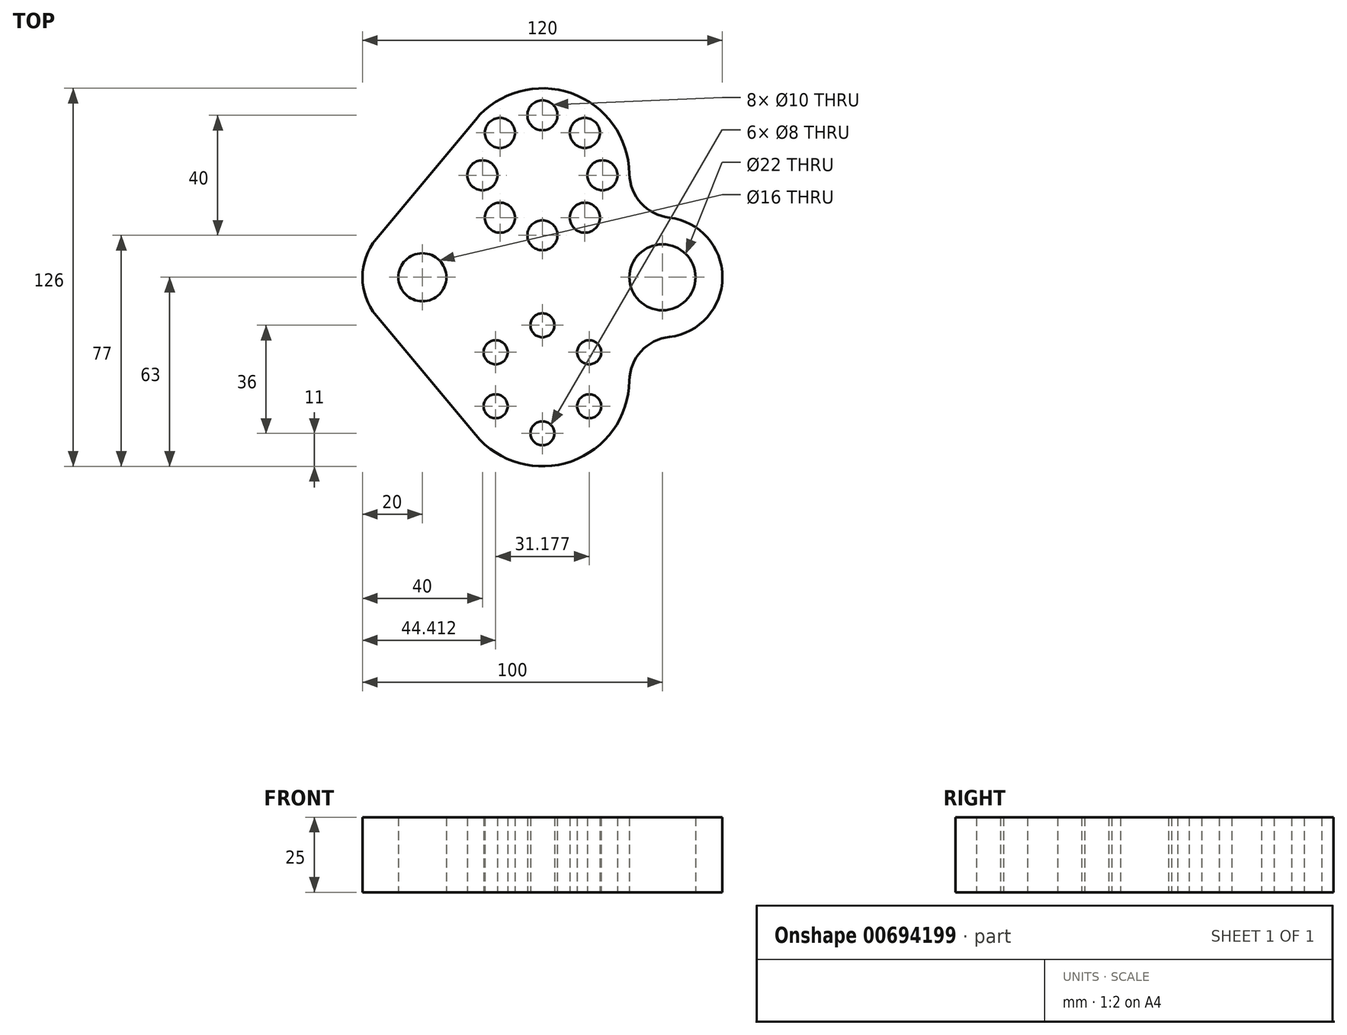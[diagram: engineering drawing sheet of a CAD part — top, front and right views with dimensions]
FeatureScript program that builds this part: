
annotation { "Feature Type Name" : "Feature", "Feature Type Description" : "" }
export const myFeature = defineFeature(function(context is Context, id is Id, definition is map)
    precondition{}
    {
        {
            var Q0;
            Q0=qCreatedBy(makeId("Top.planeOp"),FACE);
            var sketch = newSketch(context, id + "F0", { "sketchPlane" : qUnion([Q0])});
            skCircle(sketch, "E0", {"center": v(0, 34) * mm, "radius": 29 * mm});
            skCircle(sketch, "E1.MirrorC", {"center": v(0, -34) * mm, "radius": 29 * mm});
            skCircle(sketch, "E2", {"center": v(0, 54) * mm, "radius": 5 * mm});
            skCircle(sketch, "E3.1.0", {"center": v(-14.14, 48.14) * mm, "radius": 5 * mm});
            skCircle(sketch, "E3.2.0", {"center": v(-20, 34) * mm, "radius": 5 * mm});
            skCircle(sketch, "E3.3.0", {"center": v(-14.14, 19.86) * mm, "radius": 5 * mm});
            skCircle(sketch, "E3.4.0", {"center": v(0, 14) * mm, "radius": 5 * mm});
            skCircle(sketch, "E3.5.0", {"center": v(14.14, 19.86) * mm, "radius": 5 * mm});
            skCircle(sketch, "E3.6.0", {"center": v(20, 34) * mm, "radius": 5 * mm});
            skCircle(sketch, "E3.7.0", {"center": v(14.14, 48.14) * mm, "radius": 5 * mm});
            skLineSegment(sketch, "E4", {"start": v(0, -48) * mm, "end": v(0, -52) * mm});
            skCircle(sketch, "E5", {"center": v(0, -52) * mm, "radius": 4 * mm});
            skCircle(sketch, "E6.1.0", {"center": v(15.59, -43) * mm, "radius": 4 * mm});
            skCircle(sketch, "E6.2.0", {"center": v(15.59, -25) * mm, "radius": 4 * mm});
            skCircle(sketch, "E6.3.0", {"center": v(0, -16) * mm, "radius": 4 * mm});
            skCircle(sketch, "E6.4.0", {"center": v(-15.59, -25) * mm, "radius": 4 * mm});
            skCircle(sketch, "E6.5.0", {"center": v(-15.59, -43) * mm, "radius": 4 * mm});
            skCircle(sketch, "E7", {"center": v(-40, 0) * mm, "radius": 8 * mm});
            skArc(sketch, "E8", {"start": v(-55.37, 12.8) * mm, "mid": v(-60, 0) * mm, "end": v(-55.37, -12.8) * mm});
            skLineSegment(sketch, "E9", {"start": v(-55.37, 12.8) * mm, "end": v(-22.3, 52.55) * mm});
            skLineSegment(sketch, "E10.MirrorCS", {"start": v(-55.37, -12.8) * mm, "end": v(-22.3, -52.55) * mm});
            skCircle(sketch, "E11", {"center": v(40, 0) * mm, "radius": 11 * mm});
            skArc(sketch, "E12", {"start": v(42.28, -19.87) * mm, "mid": v(60, 0) * mm, "end": v(42.28, 19.87) * mm});
            skArc(sketch, "E13", {"start": v(29, 34.5) * mm, "mid": v(32.89, 24.7) * mm, "end": v(42.28, 19.87) * mm});
            skArc(sketch, "E14.MirrorCS", {"start": v(29, -34.5) * mm, "mid": v(32.89, -24.7) * mm, "end": v(42.28, -19.87) * mm});
            skSolve(sketch);
        }
        {
            var Q0;
            Q0=makeQuery(id+"F0.imprint","IMPRINT",FACE,{"disambiguationData":[TD([[makeQuery(id+"F0.imprint","IMPRINT",EDGE,{"derivedFrom":sQuery(id+"F0.wireOp",EDGE,"E7")}),-1.0]])]});
            var Q1;
            Q1=makeQuery(id+"F0.imprint","IMPRINT",FACE,{"disambiguationData":[TD([[makeQuery(id+"F0.imprint","IMPRINT",EDGE,{"derivedFrom":sQuery(id+"F0.wireOp",EDGE,"E5")}),-1.0]])]});
            var Q2;
            Q2=makeQuery(id+"F0.imprint","IMPRINT",FACE,{"disambiguationData":[TD([[makeQuery(id+"F0.imprint","IMPRINT",EDGE,{"derivedFrom":sQuery(id+"F0.wireOp",EDGE,"E2")}),-1.0]])]});
            extrude(context, id + "F1", {"entities" : qUnion([Q0, Q1, Q2]), "depth" : 25 * mm, "offsetDistance" : 25 * mm});
        }
    });
